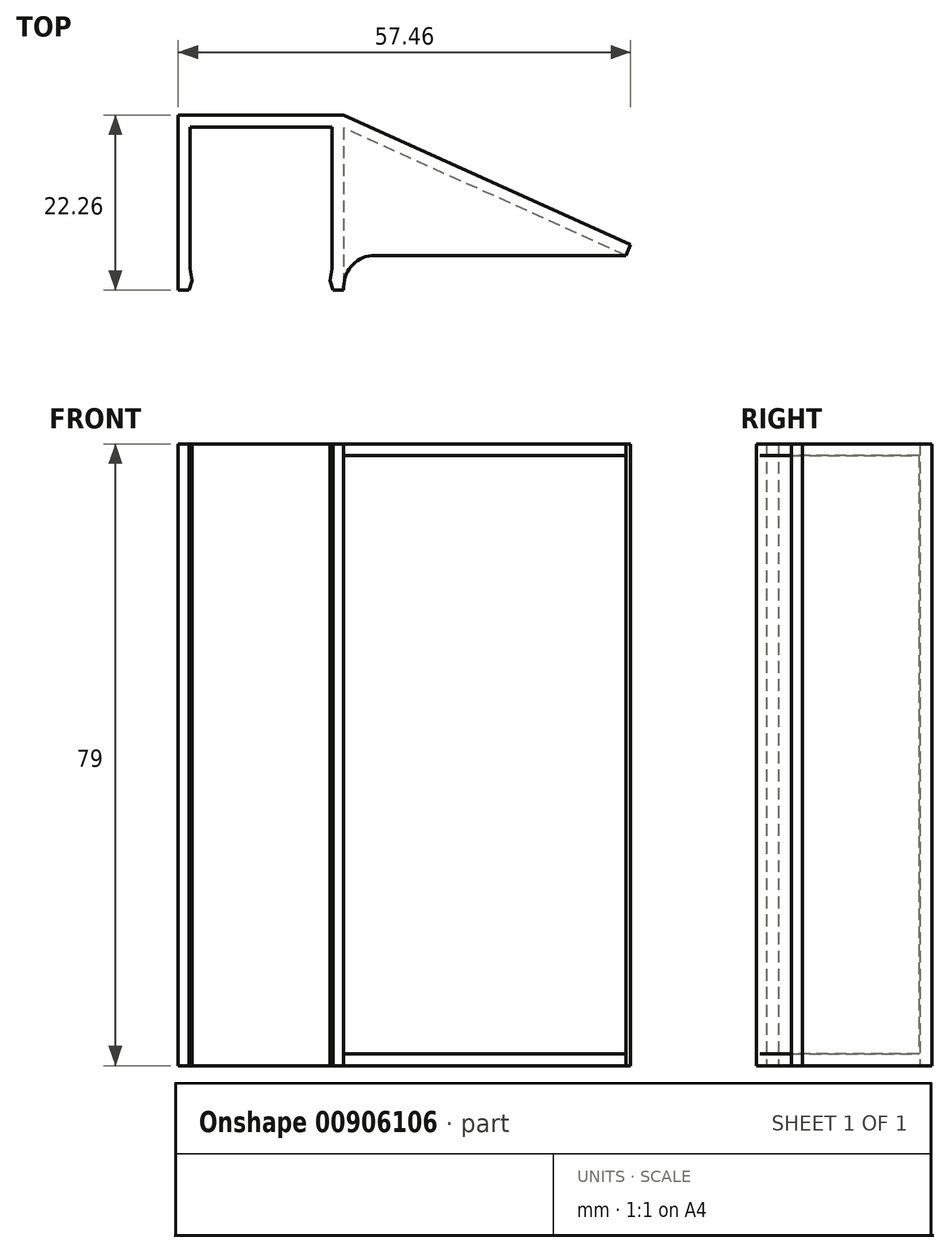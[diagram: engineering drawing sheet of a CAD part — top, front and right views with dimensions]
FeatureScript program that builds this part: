
annotation { "Feature Type Name" : "Feature", "Feature Type Description" : "" }
export const myFeature = defineFeature(function(context is Context, id is Id, definition is map)
    precondition{}
    {
        {
            var Q0;
            Q0=qCreatedBy(makeId("Top.planeOp"),FACE);
            var sketch = newSketch(context, id + "F0", { "sketchPlane" : qUnion([Q0])});
            skLineSegment(sketch, "E0.bottom", {"start": v(-9, 9) * mm, "end": v(9, 9) * mm});
            skLineSegment(sketch, "E0.left", {"start": v(-9, 9) * mm, "end": v(-9, -9) * mm});
            skLineSegment(sketch, "E0.right", {"start": v(9, 9) * mm, "end": v(9, -9) * mm});
            skPoint(sketch, "E0.middle", {"position": v(0, 0) * mm});
            skLineSegment(sketch, "E1.bottom", {"start": v(-10.5, 10.5) * mm, "end": v(10.5, 10.5) * mm});
            skLineSegment(sketch, "E1.left", {"start": v(-10.5, 10.5) * mm, "end": v(-10.5, -11.76) * mm});
            skLineSegment(sketch, "E1.right", {"start": v(10.5, -11.32) * mm, "end": v(10.5, -11.76) * mm});
            skLineSegment(sketch, "E2", {"start": v(9, -9) * mm, "end": v(8.75, -10.5) * mm});
            skLineSegment(sketch, "E3", {"start": v(0, 11.41) * mm, "end": v(0, -13.7) * mm, "construction": true});
            skPoint(sketch, "E3.startSnap0", {"position": v(0, 10.5) * mm});
            skPoint(sketch, "E3.endSnap0", {"position": v(0, 9) * mm});
            skLineSegment(sketch, "E4.MirrorCS", {"start": v(-9, -9) * mm, "end": v(-8.75, -10.5) * mm});
            skLineSegment(sketch, "E5", {"start": v(10.5, 10.5) * mm, "end": v(46.96, -5.95) * mm});
            skLineSegment(sketch, "E6", {"start": v(46.96, -5.95) * mm, "end": v(46.34, -7.32) * mm});
            skLineSegment(sketch, "E7", {"start": v(46.34, -7.32) * mm, "end": v(10.5, 8.85) * mm});
            skLineSegment(sketch, "E8", {"start": v(-8.75, -10.5) * mm, "end": v(-9.17, -11.76) * mm});
            skLineSegment(sketch, "E9", {"start": v(-9.17, -11.76) * mm, "end": v(-10.5, -11.76) * mm});
            skLineSegment(sketch, "E10.MirrorCS", {"start": v(8.75, -10.5) * mm, "end": v(9.17, -11.76) * mm});
            skLineSegment(sketch, "E11.MirrorCS", {"start": v(9.17, -11.76) * mm, "end": v(10.5, -11.76) * mm});
            skPoint(sketch, "E12.orphan", {"position": v(-10.5, -10.5) * mm});
            skPoint(sketch, "E13.orphan", {"position": v(10.5, -10.5) * mm});
            skLineSegment(sketch, "E14", {"start": v(46.34, -7.32) * mm, "end": v(14.5, -7.32) * mm});
            skArc(sketch, "E15.filletArc", {"start": v(14.5, -7.32) * mm, "mid": v(11.67, -8.5) * mm, "end": v(10.5, -11.32) * mm});
            skLineSegment(sketch, "E16", {"start": v(10.5, 8.85) * mm, "end": v(10.5, -11.32) * mm});
            skSolve(sketch);
        }
        {
            var Q0;
            Q0=makeQuery(id+"F0.imprint","IMPRINT",FACE,{"disambiguationData":[TD([[makeQuery(id+"F0.imprint","IMPRINT",EDGE,{"derivedFrom":sQuery(id+"F0.wireOp",EDGE,"E0.bottom")}),1.0]])]});
            extrude(context, id + "F1", {"entities" : qUnion([Q0]), "depth" : 79 * mm, "offsetDistance" : 25 * mm});
        }
        {
            var Q0;
            Q0=makeQuery(id+"F1.opExtrude","CAP_FACE",FACE,{"disambiguationData":[OSD([sQuery(id+"F0.wireOp",EDGE,"E0.bottom"),sQuery(id+"F0.wireOp",EDGE,"E0.left"),sQuery(id+"F0.wireOp",EDGE,"E0.right"),sQuery(id+"F0.wireOp",EDGE,"E1.bottom"),sQuery(id+"F0.wireOp",EDGE,"E1.left"),sQuery(id+"F0.wireOp",EDGE,"E1.right"),sQuery(id+"F0.wireOp",EDGE,"E2"),sQuery(id+"F0.wireOp",EDGE,"E4.MirrorCS"),sQuery(id+"F0.wireOp",EDGE,"E5"),sQuery(id+"F0.wireOp",EDGE,"E6"),sQuery(id+"F0.wireOp",EDGE,"E7"),sQuery(id+"F0.wireOp",EDGE,"E8"),sQuery(id+"F0.wireOp",EDGE,"E9"),sQuery(id+"F0.wireOp",EDGE,"E10.MirrorCS"),sQuery(id+"F0.wireOp",EDGE,"E11.MirrorCS")])],"isStart":false});
            cPlane(context, id + "F2", {"entities" : qUnion([Q0]), "cplaneType" : CPlaneType.OFFSET, "offset" : 0 * mm, "width" : 150 * mm, "height" : 150 * mm});
        }
        {
            var Q0;
            Q0=qCreatedBy(id+"F2.planeOp",FACE);
            var sketch = newSketch(context, id + "F3", { "sketchPlane" : qUnion([Q0])});
            skLineSegment(sketch, "E17.bottom", {"start": v(-9, 9) * mm, "end": v(9, 9) * mm});
            skLineSegment(sketch, "E17.left", {"start": v(-9, 9) * mm, "end": v(-9, -9) * mm});
            skLineSegment(sketch, "E17.right", {"start": v(9, 9) * mm, "end": v(9, -9) * mm});
            skPoint(sketch, "E17.middle", {"position": v(0, 0) * mm});
            skLineSegment(sketch, "E18.bottom", {"start": v(-10.5, 10.5) * mm, "end": v(10.5, 10.5) * mm});
            skLineSegment(sketch, "E18.left", {"start": v(-10.5, 10.5) * mm, "end": v(-10.5, -11.76) * mm});
            skLineSegment(sketch, "E18.right", {"start": v(10.5, -11.32) * mm, "end": v(10.5, -11.76) * mm});
            skLineSegment(sketch, "E19", {"start": v(9, -9) * mm, "end": v(8.75, -10.5) * mm});
            skLineSegment(sketch, "E20", {"start": v(0, 11.43) * mm, "end": v(0, -13.68) * mm, "construction": true});
            skPoint(sketch, "E20.startSnap0", {"position": v(0, 10.5) * mm});
            skPoint(sketch, "E20.endSnap0", {"position": v(0, 9) * mm});
            skLineSegment(sketch, "E21.MirrorCS", {"start": v(-9, -9) * mm, "end": v(-8.75, -10.5) * mm});
            skLineSegment(sketch, "E22", {"start": v(10.5, 10.5) * mm, "end": v(46.96, -5.95) * mm});
            skLineSegment(sketch, "E23", {"start": v(46.96, -5.95) * mm, "end": v(46.34, -7.32) * mm});
            skLineSegment(sketch, "E24", {"start": v(46.34, -7.32) * mm, "end": v(10.5, 8.85) * mm});
            skLineSegment(sketch, "E25", {"start": v(-8.75, -10.5) * mm, "end": v(-9.17, -11.76) * mm});
            skLineSegment(sketch, "E26", {"start": v(-9.17, -11.76) * mm, "end": v(-10.5, -11.76) * mm});
            skLineSegment(sketch, "E27.MirrorCS", {"start": v(8.75, -10.5) * mm, "end": v(9.17, -11.76) * mm});
            skLineSegment(sketch, "E28.MirrorCS", {"start": v(9.17, -11.76) * mm, "end": v(10.5, -11.76) * mm});
            skPoint(sketch, "E29.orphan", {"position": v(-10.5, -10.5) * mm});
            skPoint(sketch, "E30.orphan", {"position": v(10.5, -10.5) * mm});
            skLineSegment(sketch, "E31", {"start": v(46.34, -7.32) * mm, "end": v(14.5, -7.32) * mm});
            skPoint(sketch, "E32", {"position": v(-10.5, -11.76) * mm});
            skArc(sketch, "E33.filletArc", {"start": v(14.5, -7.32) * mm, "mid": v(11.67, -8.5) * mm, "end": v(10.5, -11.32) * mm});
            skSolve(sketch);
        }
        {
            var Q0;
            Q0=makeQuery(id+"F3.imprint","IMPRINT",FACE,{"disambiguationData":[TD([[makeQuery(id+"F3.imprint","IMPRINT",EDGE,{"derivedFrom":sQuery(id+"F3.wireOp",EDGE,"E17.bottom")}),1.0]])]});
            extrude(context, id + "F4", {"entities" : qUnion([Q0]), "operationType" : NewBodyOperationType.ADD, "oppositeDirection" : true, "depth" : 1.5 * mm, "offsetDistance" : 25 * mm});
        }
        {
            var Q0;
            Q0=makeQuery(id+"F0.imprint","IMPRINT",FACE,{"disambiguationData":[TD([[makeQuery(id+"F0.imprint","IMPRINT",EDGE,{"derivedFrom":sQuery(id+"F0.wireOp",EDGE,"E7")}),1.0]])]});
            extrude(context, id + "F5", {"entities" : qUnion([Q0]), "operationType" : NewBodyOperationType.ADD, "depth" : 1.5 * mm, "offsetDistance" : 25 * mm});
        }
    });
